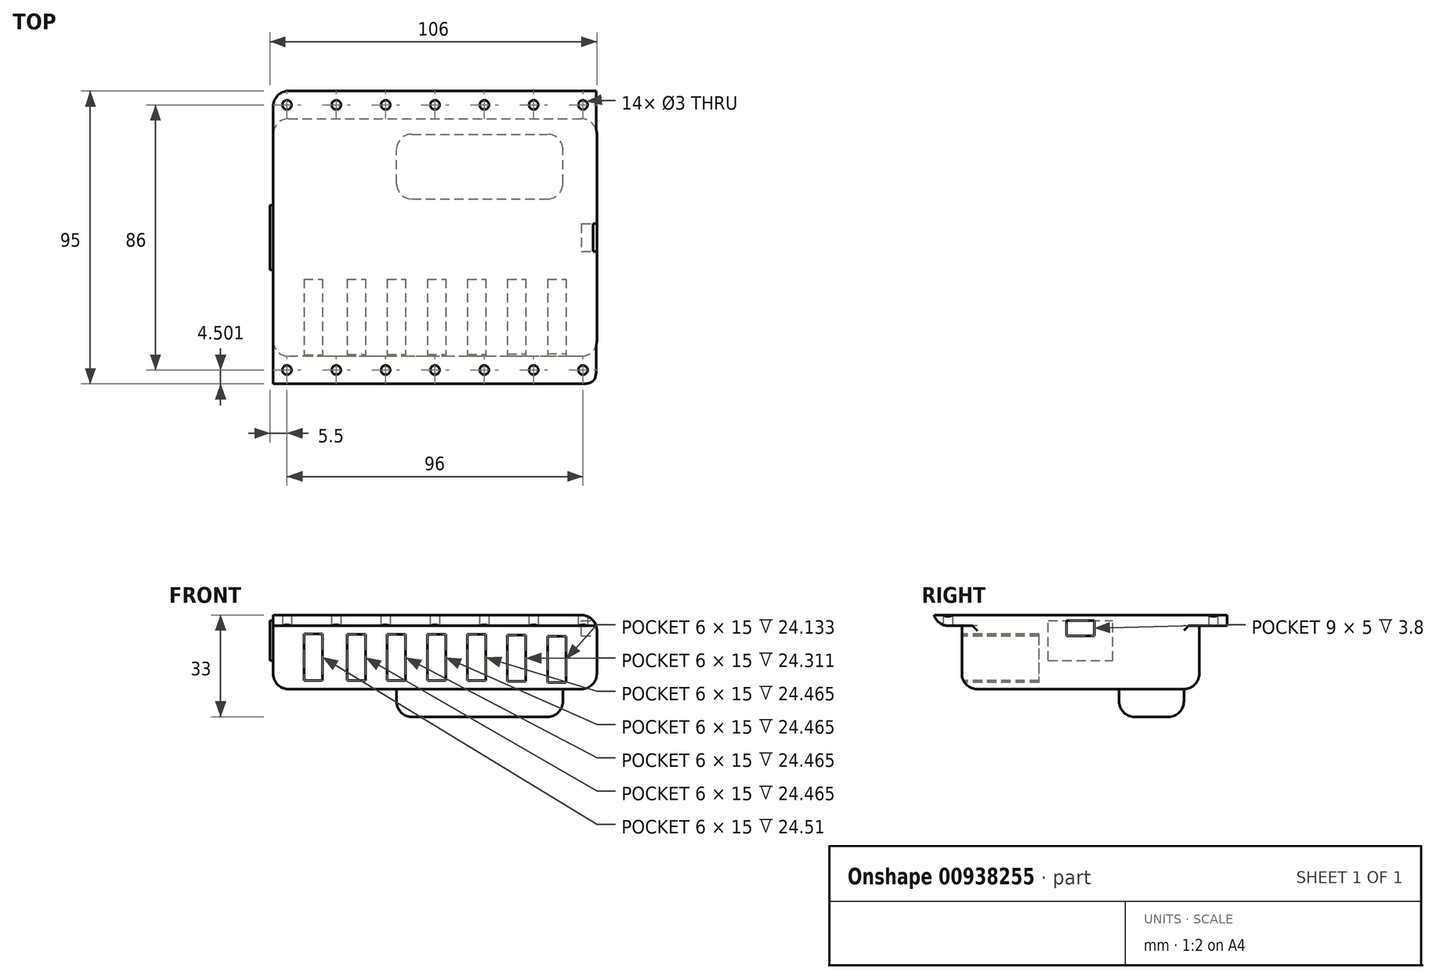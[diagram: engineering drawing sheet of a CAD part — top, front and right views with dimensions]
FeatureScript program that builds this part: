
annotation { "Feature Type Name" : "Feature", "Feature Type Description" : "" }
export const myFeature = defineFeature(function(context is Context, id is Id, definition is map)
    precondition{}
    {
        {
            var Q0;
            Q0=qCreatedBy(makeId("Top.planeOp"),FACE);
            var sketch = newSketch(context, id + "F0", { "sketchPlane" : qUnion([Q0])});
            skLineSegment(sketch, "E0.bottom", {"start": v(-52.9, 57.54) * mm, "end": v(52.1, 57.54) * mm});
            skLineSegment(sketch, "E0.top", {"start": v(-52.9, -37.46) * mm, "end": v(52.1, -37.46) * mm});
            skLineSegment(sketch, "E0.left", {"start": v(-52.9, 57.54) * mm, "end": v(-52.9, -37.46) * mm});
            skLineSegment(sketch, "E0.right", {"start": v(52.1, 57.54) * mm, "end": v(52.1, -37.46) * mm});
            skSolve(sketch);
        }
        {
            var Q0;
            Q0=makeQuery(id+"F0.imprint","IMPRINT",FACE,{"disambiguationData":[TD([[makeQuery(id+"F0.imprint","IMPRINT",EDGE,{"derivedFrom":sQuery(id+"F0.wireOp",EDGE,"E0.bottom")}),-1.0]])]});
            extrude(context, id + "F1", {"entities" : qUnion([Q0]), "depth" : 3.5 * mm, "symmetric" : true});
        }
        {
            var Q0;
            Q0=makeQuery(id+"F1.opExtrude","CAP_FACE",FACE,{"disambiguationData":[OSD([sQuery(id+"F0.wireOp",EDGE,"E0.bottom"),sQuery(id+"F0.wireOp",EDGE,"E0.top"),sQuery(id+"F0.wireOp",EDGE,"E0.left"),sQuery(id+"F0.wireOp",EDGE,"E0.right")])],"isStart":true});
            var sketch = newSketch(context, id + "F2", { "sketchPlane" : qUnion([Q0])});
            skLineSegment(sketch, "E1.bottom", {"start": v(-52.9, 28.46) * mm, "end": v(52.1, 28.46) * mm});
            skLineSegment(sketch, "E1.top", {"start": v(-52.9, -48.54) * mm, "end": v(52.1, -48.54) * mm});
            skLineSegment(sketch, "E1.left", {"start": v(-52.9, 28.46) * mm, "end": v(-52.9, -48.54) * mm});
            skLineSegment(sketch, "E1.right", {"start": v(52.1, 28.46) * mm, "end": v(52.1, -48.54) * mm});
            skPoint(sketch, "E2", {"position": v(52.1, 37.46) * mm});
            skPoint(sketch, "E3", {"position": v(52.1, -57.54) * mm});
            skSolve(sketch);
        }
        {
            var Q0;
            Q0=qSketchRegion(id+"F2",true);
            extrude(context, id + "F3", {"entities" : qUnion([Q0]), "operationType" : NewBodyOperationType.ADD, "depth" : 20.5 * mm});
        }
        {
            var Q0;
            Q0=makeQuery(id+"F3.opExtrude","CAP_FACE",FACE,{"disambiguationData":[OSD([sQuery(id+"F2.wireOp",EDGE,"E1.bottom"),sQuery(id+"F2.wireOp",EDGE,"E1.top"),sQuery(id+"F2.wireOp",EDGE,"E1.left"),sQuery(id+"F2.wireOp",EDGE,"E1.right")])],"isStart":false});
            var sketch = newSketch(context, id + "F4", { "sketchPlane" : qUnion([Q0])});
            skLineSegment(sketch, "E4.bottom", {"start": v(-12.9, -22.54) * mm, "end": v(41.1, -22.54) * mm});
            skLineSegment(sketch, "E4.top", {"start": v(-12.9, -43.54) * mm, "end": v(41.1, -43.54) * mm});
            skLineSegment(sketch, "E4.left", {"start": v(-12.9, -22.54) * mm, "end": v(-12.9, -43.54) * mm});
            skLineSegment(sketch, "E4.right", {"start": v(41.1, -22.54) * mm, "end": v(41.1, -43.54) * mm});
            skSolve(sketch);
        }
        {
            var Q0;
            Q0=qSketchRegion(id+"F4",true);
            extrude(context, id + "F5", {"entities" : qUnion([Q0]), "operationType" : NewBodyOperationType.ADD, "depth" : 9 * mm});
        }
        {
            var Q0;
            Q0=makeQuery(id+"F3.boolean.opBoolean","MERGE",FACE,{"derivedFrom":[makeQuery(id+"F1.opExtrude","SWEPT_FACE",FACE,{"disambiguationData":[OSD([sQuery(id+"F0.wireOp",EDGE,"E0.right")])]}),makeQuery(id+"F3.opExtrude","SWEPT_FACE",FACE,{"disambiguationData":[OSD([sQuery(id+"F2.wireOp",EDGE,"E1.right")])]})]});
            var sketch = newSketch(context, id + "F6", { "sketchPlane" : qUnion([Q0])});
            skPoint(sketch, "E5", {"position": v(10.04, 1.75) * mm});
            skLineSegment(sketch, "E6.bottom", {"start": v(14.54, -5) * mm, "end": v(5.54, -5) * mm});
            skLineSegment(sketch, "E6.top", {"start": v(14.54, 0) * mm, "end": v(5.54, 0) * mm});
            skLineSegment(sketch, "E6.left", {"start": v(14.54, -5) * mm, "end": v(14.54, 0) * mm});
            skLineSegment(sketch, "E6.right", {"start": v(5.54, -5) * mm, "end": v(5.54, 0) * mm});
            skSolve(sketch);
        }
        {
            var Q0;
            Q0=makeQuery(id+"F6.imprint","IMPRINT",FACE,{"disambiguationData":[TD([[makeQuery(id+"F6.imprint","IMPRINT",EDGE,{"derivedFrom":sQuery(id+"F6.wireOp",EDGE,"E6.bottom")}),-1.0]])]});
            extrude(context, id + "F7", {"entities" : qUnion([Q0]), "operationType" : NewBodyOperationType.REMOVE, "oppositeDirection" : true, "depth" : 5 * mm});
        }
        {
            var Q0;
            Q0=makeQuery(id+"F3.boolean.opBoolean","MERGE",FACE,{"derivedFrom":[makeQuery(id+"F1.opExtrude","SWEPT_FACE",FACE,{"disambiguationData":[OSD([sQuery(id+"F0.wireOp",EDGE,"E0.left")])]}),makeQuery(id+"F3.opExtrude","SWEPT_FACE",FACE,{"disambiguationData":[OSD([sQuery(id+"F2.wireOp",EDGE,"E1.left")])]})]});
            var sketch = newSketch(context, id + "F8", { "sketchPlane" : qUnion([Q0])});
            skLineSegment(sketch, "E7.bottom", {"start": v(0.46, -13) * mm, "end": v(-20.54, -13) * mm});
            skLineSegment(sketch, "E7.top", {"start": v(0.46, 0) * mm, "end": v(-20.54, 0) * mm});
            skLineSegment(sketch, "E7.left", {"start": v(0.46, -13) * mm, "end": v(0.46, 0) * mm});
            skLineSegment(sketch, "E7.right", {"start": v(-20.54, -13) * mm, "end": v(-20.54, 0) * mm});
            skSolve(sketch);
        }
        {
            var Q0;
            Q0=qSketchRegion(id+"F8",true);
            extrude(context, id + "F9", {"entities" : qUnion([Q0]), "operationType" : NewBodyOperationType.ADD, "depth" : 1 * mm});
        }
        {
            var Q0;
            {var subQ0=sQuery(id+"F0.wireOp",EDGE,"E0.right");var subQ1=sQuery(id+"F0.wireOp",EDGE,"E0.left");var subQ2=sQuery(id+"F0.wireOp",EDGE,"E0.top");Q0=makeQuery(id+"F3.boolean.opBoolean","SPLIT",FACE,{"disambiguationData":[TD([makeQuery(id+"F1.opExtrude","SWEPT_FACE",FACE,{"disambiguationData":[OSD([subQ2])]})])],"derivedFrom":makeQuery(id+"F1.opExtrude","CAP_FACE",FACE,{"disambiguationData":[OSD([sQuery(id+"F0.wireOp",EDGE,"E0.bottom"),subQ2,subQ1,subQ0])],"isStart":true})});}
            var sketch = newSketch(context, id + "F10", { "sketchPlane" : qUnion([Q0])});
            skLineSegment(sketch, "E8", {"start": v(52.1, 32.96) * mm, "end": v(-52.9, 32.96) * mm});
            skPoint(sketch, "E9", {"position": v(-0.4, 32.96) * mm});
            skPoint(sketch, "E10", {"position": v(-16.4, 32.96) * mm});
            skPoint(sketch, "E11", {"position": v(-32.4, 32.96) * mm});
            skPoint(sketch, "E12", {"position": v(-48.4, 32.96) * mm});
            skPoint(sketch, "E13", {"position": v(15.6, 32.96) * mm});
            skPoint(sketch, "E14", {"position": v(31.6, 32.96) * mm});
            skPoint(sketch, "E15", {"position": v(47.6, 32.96) * mm});
            skSolve(sketch);
        }
        {
            var Q0;
            Q0=sQuery(id+"F10.wireOp",VERTEX,"E15");
            var Q1;
            Q1=sQuery(id+"F10.wireOp",VERTEX,"E14");
            var Q2;
            Q2=sQuery(id+"F10.wireOp",VERTEX,"E13");
            var Q3;
            Q3=sQuery(id+"F10.wireOp",VERTEX,"E9");
            var Q4;
            Q4=sQuery(id+"F10.wireOp",VERTEX,"E10");
            var Q5;
            Q5=sQuery(id+"F10.wireOp",VERTEX,"E11");
            var Q6;
            Q6=sQuery(id+"F10.wireOp",VERTEX,"E12");
            var Q7;
            Q7=makeQuery(id+"F1.opExtrude","SWEPT_BODY",BODY,{"disambiguationData":[OSD([sQuery(id+"F0.wireOp",EDGE,"E0.bottom"),sQuery(id+"F0.wireOp",EDGE,"E0.top"),sQuery(id+"F0.wireOp",EDGE,"E0.left"),sQuery(id+"F0.wireOp",EDGE,"E0.right")])]});
            hole(context, id + "F11", {"style" : HoleStyle.SIMPLE, "endStyle" : HoleEndStyle.THROUGH, "holeDiameter" : 3 * mm, "locations" : qUnion([Q0, Q1, Q2, Q3, Q4, Q5, Q6]), "scope" : qUnion([Q7]), "isTappedThrough" : true});
        }
        {
            var Q0;
            {var subQ0=sQuery(id+"F0.wireOp",EDGE,"E0.right");var subQ1=sQuery(id+"F0.wireOp",EDGE,"E0.left");var subQ2=sQuery(id+"F0.wireOp",EDGE,"E0.bottom");Q0=makeQuery(id+"F3.boolean.opBoolean","SPLIT",FACE,{"disambiguationData":[TD([makeQuery(id+"F1.opExtrude","SWEPT_FACE",FACE,{"disambiguationData":[OSD([subQ2])]})])],"derivedFrom":makeQuery(id+"F1.opExtrude","CAP_FACE",FACE,{"disambiguationData":[OSD([subQ2,sQuery(id+"F0.wireOp",EDGE,"E0.top"),subQ1,subQ0])],"isStart":true})});}
            var sketch = newSketch(context, id + "F12", { "sketchPlane" : qUnion([Q0])});
            skLineSegment(sketch, "E16", {"start": v(52.1, -53.04) * mm, "end": v(-52.9, -53.04) * mm});
            skPoint(sketch, "E17", {"position": v(-0.4, -53.04) * mm});
            skPoint(sketch, "E18", {"position": v(-16.4, -53.04) * mm});
            skPoint(sketch, "E19", {"position": v(-32.4, -53.04) * mm});
            skPoint(sketch, "E20", {"position": v(15.6, -53.04) * mm});
            skPoint(sketch, "E21", {"position": v(31.6, -53.04) * mm});
            skPoint(sketch, "E22", {"position": v(47.6, -53.04) * mm});
            skPoint(sketch, "E23", {"position": v(-48.4, -53.04) * mm});
            skSolve(sketch);
        }
        {
            var Q0;
            Q0=sQuery(id+"F12.wireOp",VERTEX,"E22");
            var Q1;
            Q1=sQuery(id+"F12.wireOp",VERTEX,"E21");
            var Q2;
            Q2=sQuery(id+"F12.wireOp",VERTEX,"E20");
            var Q3;
            Q3=sQuery(id+"F12.wireOp",VERTEX,"E17");
            var Q4;
            Q4=sQuery(id+"F12.wireOp",VERTEX,"E18");
            var Q5;
            Q5=sQuery(id+"F12.wireOp",VERTEX,"E19");
            var Q6;
            Q6=sQuery(id+"F12.wireOp",VERTEX,"E23");
            var Q7;
            Q7=makeQuery(id+"F1.opExtrude","SWEPT_BODY",BODY,{"disambiguationData":[OSD([sQuery(id+"F0.wireOp",EDGE,"E0.bottom"),sQuery(id+"F0.wireOp",EDGE,"E0.top"),sQuery(id+"F0.wireOp",EDGE,"E0.left"),sQuery(id+"F0.wireOp",EDGE,"E0.right")])]});
            hole(context, id + "F13", {"style" : HoleStyle.SIMPLE, "endStyle" : HoleEndStyle.THROUGH, "holeDiameter" : 3 * mm, "locations" : qUnion([Q0, Q1, Q2, Q3, Q4, Q5, Q6]), "scope" : qUnion([Q7]), "isTappedThrough" : true});
        }
        {
            var Q0;
            Q0=makeQuery(id+"F3.opExtrude","SWEPT_FACE",FACE,{"disambiguationData":[OSD([sQuery(id+"F2.wireOp",EDGE,"E1.bottom")])]});
            var sketch = newSketch(context, id + "F14", { "sketchPlane" : qUnion([Q0])});
            skLineSegment(sketch, "E24.bottom", {"start": v(-42.9, -4.4) * mm, "end": v(-36.9, -4.4) * mm});
            skLineSegment(sketch, "E24.top", {"start": v(-42.9, -19.4) * mm, "end": v(-36.9, -19.4) * mm});
            skLineSegment(sketch, "E24.left", {"start": v(-42.9, -4.4) * mm, "end": v(-42.9, -19.4) * mm});
            skLineSegment(sketch, "E24.right", {"start": v(-36.9, -4.4) * mm, "end": v(-36.9, -19.4) * mm});
            skLineSegment(sketch, "E25.bottom", {"start": v(-28.9, -4.5) * mm, "end": v(-22.9, -4.5) * mm});
            skLineSegment(sketch, "E25.top", {"start": v(-28.9, -19.5) * mm, "end": v(-22.9, -19.5) * mm});
            skLineSegment(sketch, "E25.left", {"start": v(-28.9, -4.5) * mm, "end": v(-28.9, -19.5) * mm});
            skLineSegment(sketch, "E25.right", {"start": v(-22.9, -4.5) * mm, "end": v(-22.9, -19.5) * mm});
            skLineSegment(sketch, "E26.bottom", {"start": v(-15.9, -4.5) * mm, "end": v(-9.9, -4.5) * mm});
            skLineSegment(sketch, "E26.top", {"start": v(-15.9, -19.5) * mm, "end": v(-9.9, -19.5) * mm});
            skLineSegment(sketch, "E26.left", {"start": v(-15.9, -4.5) * mm, "end": v(-15.9, -19.5) * mm});
            skLineSegment(sketch, "E26.right", {"start": v(-9.9, -4.5) * mm, "end": v(-9.9, -19.5) * mm});
            skLineSegment(sketch, "E27.bottom", {"start": v(-2.9, -4.5) * mm, "end": v(3.1, -4.5) * mm});
            skLineSegment(sketch, "E27.top", {"start": v(-2.9, -19.5) * mm, "end": v(3.1, -19.5) * mm});
            skLineSegment(sketch, "E27.left", {"start": v(-2.9, -4.5) * mm, "end": v(-2.9, -19.5) * mm});
            skLineSegment(sketch, "E27.right", {"start": v(3.1, -4.5) * mm, "end": v(3.1, -19.5) * mm});
            skLineSegment(sketch, "E28.bottom", {"start": v(10.1, -4.5) * mm, "end": v(16.1, -4.5) * mm});
            skLineSegment(sketch, "E28.top", {"start": v(10.1, -19.5) * mm, "end": v(16.1, -19.5) * mm});
            skLineSegment(sketch, "E28.left", {"start": v(10.1, -4.5) * mm, "end": v(10.1, -19.5) * mm});
            skLineSegment(sketch, "E28.right", {"start": v(16.1, -4.5) * mm, "end": v(16.1, -19.5) * mm});
            skLineSegment(sketch, "E29.bottom", {"start": v(23.1, -4.78) * mm, "end": v(29.1, -4.78) * mm});
            skLineSegment(sketch, "E29.top", {"start": v(23.1, -19.78) * mm, "end": v(29.1, -19.78) * mm});
            skLineSegment(sketch, "E29.left", {"start": v(23.1, -4.78) * mm, "end": v(23.1, -19.78) * mm});
            skLineSegment(sketch, "E29.right", {"start": v(29.1, -4.78) * mm, "end": v(29.1, -19.78) * mm});
            skLineSegment(sketch, "E30.bottom", {"start": v(36.1, -5.06) * mm, "end": v(42.1, -5.06) * mm});
            skLineSegment(sketch, "E30.top", {"start": v(36.1, -20.06) * mm, "end": v(42.1, -20.06) * mm});
            skLineSegment(sketch, "E30.left", {"start": v(36.1, -5.06) * mm, "end": v(36.1, -20.06) * mm});
            skLineSegment(sketch, "E30.right", {"start": v(42.1, -5.06) * mm, "end": v(42.1, -20.06) * mm});
            skSolve(sketch);
        }
        {
            var Q0;
            Q0=qSketchRegion(id+"F14",true);
            extrude(context, id + "F15", {"entities" : qUnion([Q0]), "operationType" : NewBodyOperationType.REMOVE, "oppositeDirection" : true, "depth" : 25 * mm});
        }
        {
            var Q0;
            Q0=makeQuery(id+"F3.opExtrude","CAP_EDGE",EDGE,{"disambiguationData":[OSD([sQuery(id+"F2.wireOp",EDGE,"E1.right")])],"isStart":false});
            var Q1;
            Q1=makeQuery(id+"F3.opExtrude","CAP_EDGE",EDGE,{"disambiguationData":[OSD([sQuery(id+"F2.wireOp",EDGE,"E1.bottom")])],"isStart":false});
            var Q2;
            Q2=makeQuery(id+"F3.opExtrude","SWEPT_EDGE",EDGE,{"disambiguationData":[OSD([sQuery(id+"F0.wireOp",EDGE,"E0.right"),sQuery(id+"F2.wireOp",EDGE,"E1.bottom"),sQuery(id+"F2.wireOp",EDGE,"E1.right")])]});
            var Q3;
            Q3=makeQuery(id+"F5.opExtrude","CAP_EDGE",EDGE,{"disambiguationData":[OSD([sQuery(id+"F4.wireOp",EDGE,"E4.bottom")])],"isStart":false});
            var Q4;
            Q4=makeQuery(id+"F5.opExtrude","CAP_EDGE",EDGE,{"disambiguationData":[OSD([sQuery(id+"F4.wireOp",EDGE,"E4.right")])],"isStart":false});
            var Q5;
            Q5=makeQuery(id+"F5.opExtrude","CAP_EDGE",EDGE,{"disambiguationData":[OSD([sQuery(id+"F4.wireOp",EDGE,"E4.left")])],"isStart":false});
            var Q6;
            Q6=makeQuery(id+"F5.opExtrude","CAP_EDGE",EDGE,{"disambiguationData":[OSD([sQuery(id+"F4.wireOp",EDGE,"E4.top")])],"isStart":false});
            var Q7;
            Q7=makeQuery(id+"F5.opExtrude","SWEPT_EDGE",EDGE,{"disambiguationData":[OSD([sQuery(id+"F4.wireOp",EDGE,"E4.bottom"),sQuery(id+"F4.wireOp",EDGE,"E4.right")])]});
            var Q8;
            Q8=makeQuery(id+"F5.opExtrude","SWEPT_EDGE",EDGE,{"disambiguationData":[OSD([sQuery(id+"F4.wireOp",EDGE,"E4.top"),sQuery(id+"F4.wireOp",EDGE,"E4.right")])]});
            var Q9;
            Q9=makeQuery(id+"F3.opExtrude","SWEPT_EDGE",EDGE,{"disambiguationData":[OSD([sQuery(id+"F0.wireOp",EDGE,"E0.right"),sQuery(id+"F2.wireOp",EDGE,"E1.top"),sQuery(id+"F2.wireOp",EDGE,"E1.right")])]});
            var Q10;
            Q10=makeQuery(id+"F3.opExtrude","CAP_EDGE",EDGE,{"disambiguationData":[OSD([sQuery(id+"F2.wireOp",EDGE,"E1.left")])],"isStart":false});
            var Q11;
            Q11=makeQuery(id+"F3.opExtrude","CAP_EDGE",EDGE,{"disambiguationData":[OSD([sQuery(id+"F2.wireOp",EDGE,"E1.top")])],"isStart":false});
            fillet(context, id + "F16", {"entities" : qUnion([Q0, Q1, Q2, Q3, Q4, Q5, Q6, Q7, Q8, Q9, Q10, Q11]), "radius" : 5 * mm, "tangentPropagation" : true, "allowEdgeOverflow" : false});
        }
        {
            var Q0;
            Q0=makeQuery(id+"F3.opExtrude","SWEPT_EDGE",EDGE,{"disambiguationData":[OSD([sQuery(id+"F0.wireOp",EDGE,"E0.left"),sQuery(id+"F2.wireOp",EDGE,"E1.top"),sQuery(id+"F2.wireOp",EDGE,"E1.left")])]});
            var Q1;
            Q1=makeQuery(id+"F3.opExtrude","SWEPT_EDGE",EDGE,{"disambiguationData":[OSD([sQuery(id+"F0.wireOp",EDGE,"E0.left"),sQuery(id+"F2.wireOp",EDGE,"E1.bottom"),sQuery(id+"F2.wireOp",EDGE,"E1.left")])]});
            var Q2;
            Q2=makeQuery(id+"F5.opExtrude","SWEPT_EDGE",EDGE,{"disambiguationData":[OSD([sQuery(id+"F4.wireOp",EDGE,"E4.top"),sQuery(id+"F4.wireOp",EDGE,"E4.left")])]});
            var Q3;
            Q3=makeQuery(id+"F5.opExtrude","SWEPT_EDGE",EDGE,{"disambiguationData":[OSD([sQuery(id+"F4.wireOp",EDGE,"E4.bottom"),sQuery(id+"F4.wireOp",EDGE,"E4.left")])]});
            var Q4;
            Q4=makeQuery(id+"F1.opExtrude","CAP_EDGE",EDGE,{"disambiguationData":[OSD([sQuery(id+"F0.wireOp",EDGE,"E0.top")])],"isStart":true});
            var Q5;
            Q5=makeQuery(id+"F1.opExtrude","CAP_EDGE",EDGE,{"disambiguationData":[OSD([sQuery(id+"F0.wireOp",EDGE,"E0.right")])],"isStart":false});
            fillet(context, id + "F17", {"entities" : qUnion([Q0, Q1, Q2, Q3, Q4, Q5]), "radius" : 5 * mm, "tangentPropagation" : true, "allowEdgeOverflow" : false});
        }
        {
            var Q0;
            Q0=makeQuery(id+"F1.opExtrude","SWEPT_EDGE",EDGE,{"disambiguationData":[OSD([sQuery(id+"F0.wireOp",EDGE,"E0.top"),sQuery(id+"F0.wireOp",EDGE,"E0.left")])]});
            var Q1;
            Q1=makeQuery(id+"F1.opExtrude","SWEPT_EDGE",EDGE,{"disambiguationData":[OSD([sQuery(id+"F0.wireOp",EDGE,"E0.top"),sQuery(id+"F0.wireOp",EDGE,"E0.right")])]});
            var Q2;
            Q2=makeQuery(id+"F1.opExtrude","SWEPT_EDGE",EDGE,{"disambiguationData":[OSD([sQuery(id+"F0.wireOp",EDGE,"E0.bottom"),sQuery(id+"F0.wireOp",EDGE,"E0.left")])]});
            var Q3;
            Q3=makeQuery(id+"F1.opExtrude","SWEPT_EDGE",EDGE,{"disambiguationData":[OSD([sQuery(id+"F0.wireOp",EDGE,"E0.bottom"),sQuery(id+"F0.wireOp",EDGE,"E0.right")])]});
            fillet(context, id + "F18", {"entities" : qUnion([Q0, Q1, Q2, Q3]), "radius" : 5 * mm, "tangentPropagation" : true, "allowEdgeOverflow" : false});
        }
    });
